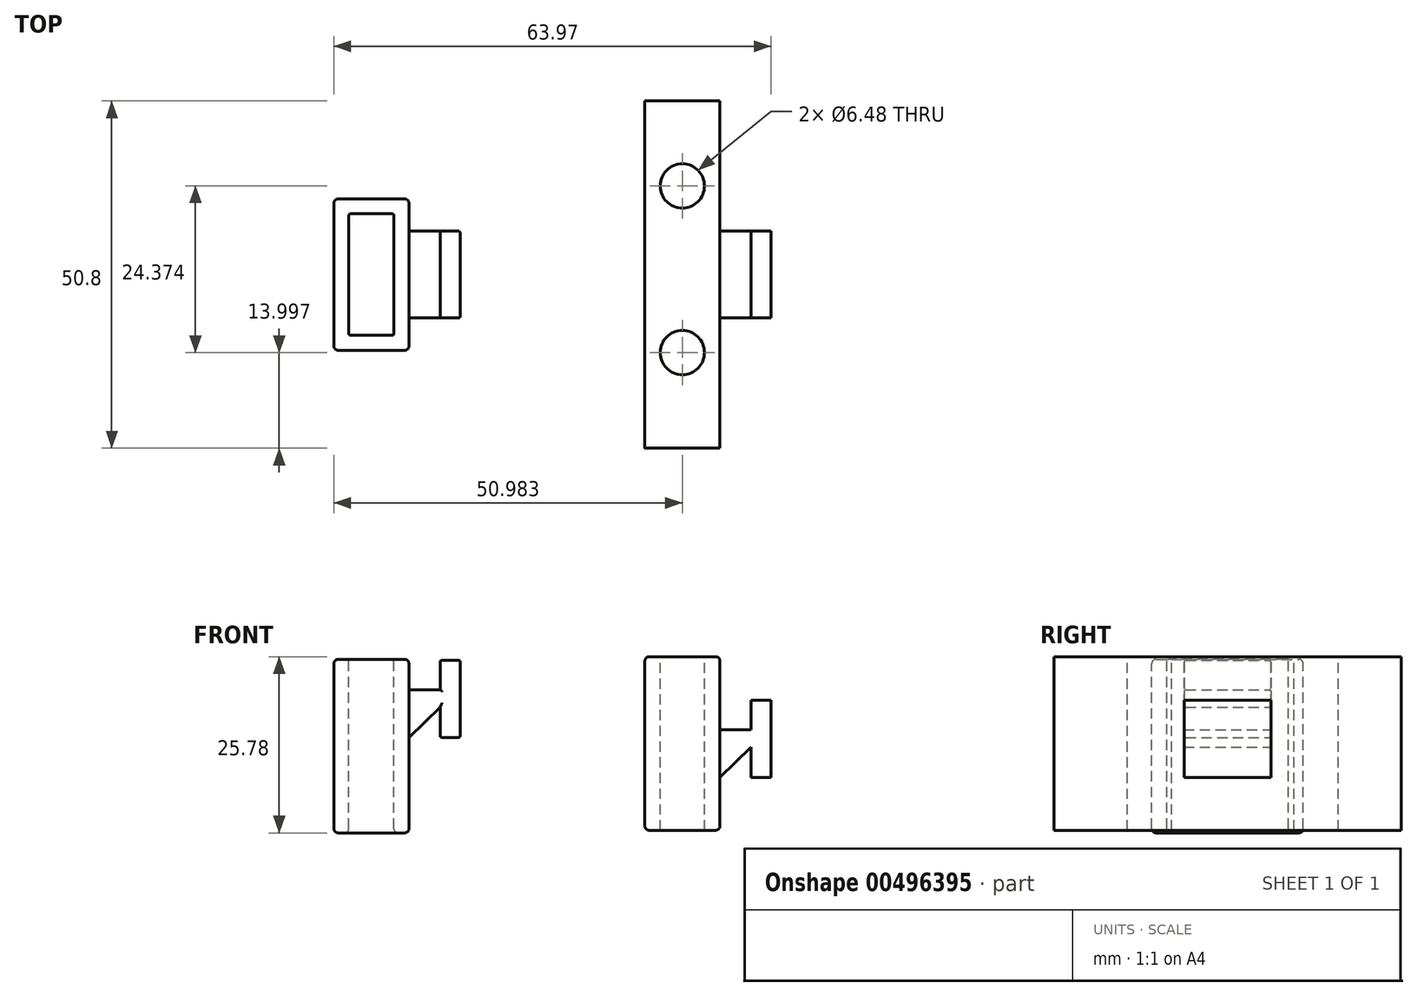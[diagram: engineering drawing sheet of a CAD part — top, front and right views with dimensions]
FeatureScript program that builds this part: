
annotation { "Feature Type Name" : "Feature", "Feature Type Description" : "" }
export const myFeature = defineFeature(function(context is Context, id is Id, definition is map)
    precondition{}
    {
        {
            var Q0;
            Q0=qCreatedBy(makeId("Front.planeOp"),FACE);
            var sketch = newSketch(context, id + "F0", { "sketchPlane" : qUnion([Q0])});
            skLineSegment(sketch, "E0", {"start": v(0, 0) * mm, "end": v(0, 11.3) * mm});
            skLineSegment(sketch, "E1", {"start": v(0, 11.3) * mm, "end": v(-2.92, 11.3) * mm});
            skLineSegment(sketch, "E2", {"start": v(-2.92, 11.3) * mm, "end": v(-2.92, 6.99) * mm});
            skLineSegment(sketch, "E3", {"start": v(-2.92, 6.99) * mm, "end": v(-7.5, 6.98) * mm});
            skLineSegment(sketch, "E4", {"start": v(-7.5, 6.99) * mm, "end": v(-7.5, 0) * mm});
            skLineSegment(sketch, "E5", {"start": v(-7.5, 0) * mm, "end": v(-2.92, 4.44) * mm});
            skLineSegment(sketch, "E6", {"start": v(-2.92, 4.44) * mm, "end": v(-2.92, 0) * mm});
            skLineSegment(sketch, "E7", {"start": v(-2.92, 0) * mm, "end": v(0, 0) * mm});
            skSolve(sketch);
        }
        {
            var Q0;
            Q0 = qSketchRegion(id + "F0", true);
            extrude(context, id + "F1", {"entities" : qUnion([Q0]), "depth" : 12.7 * mm});
        }
        {
            var Q0;
            Q0=makeQuery(id+"F1.opExtrude","CAP_FACE",FACE,{"disambiguationData":[OSD([sQuery(id+"F0.wireOp",EDGE,"E0"),sQuery(id+"F0.wireOp",EDGE,"E1"),sQuery(id+"F0.wireOp",EDGE,"E2"),sQuery(id+"F0.wireOp",EDGE,"E3"),sQuery(id+"F0.wireOp",EDGE,"E4"),sQuery(id+"F0.wireOp",EDGE,"E5"),sQuery(id+"F0.wireOp",EDGE,"E6"),sQuery(id+"F0.wireOp",EDGE,"E7")])],"isStart":true});
            var sketch = newSketch(context, id + "F2", { "sketchPlane" : qUnion([Q0])});
            skLineSegment(sketch, "E8", {"start": v(7.5, 0) * mm, "end": v(7.5, 10.8) * mm});
            skLineSegment(sketch, "E9", {"start": v(7.5, 0) * mm, "end": v(7.5, -13.34) * mm});
            skLineSegment(sketch, "E10", {"start": v(8.13, -13.97) * mm, "end": v(17.84, -13.97) * mm});
            skLineSegment(sketch, "E11", {"start": v(18.48, -13.34) * mm, "end": v(18.48, 10.8) * mm});
            skLineSegment(sketch, "E12", {"start": v(17.84, 11.43) * mm, "end": v(8.13, 11.43) * mm});
            skPoint(sketch, "E13.visualSharp", {"position": v(7.5, 11.43) * mm});
            skArc(sketch, "E13.filletArc", {"start": v(8.13, 11.43) * mm, "mid": v(7.68, 11.24) * mm, "end": v(7.5, 10.8) * mm});
            skPoint(sketch, "E14.visualSharp", {"position": v(18.48, 11.43) * mm});
            skArc(sketch, "E14.filletArc", {"start": v(18.48, 10.8) * mm, "mid": v(18.3, 11.24) * mm, "end": v(17.84, 11.43) * mm});
            skPoint(sketch, "E15.visualSharp", {"position": v(18.48, -13.97) * mm});
            skArc(sketch, "E15.filletArc", {"start": v(17.84, -13.97) * mm, "mid": v(18.3, -13.78) * mm, "end": v(18.48, -13.34) * mm});
            skPoint(sketch, "E16.visualSharp", {"position": v(7.5, -13.97) * mm});
            skArc(sketch, "E16.filletArc", {"start": v(7.5, -13.34) * mm, "mid": v(7.68, -13.78) * mm, "end": v(8.13, -13.97) * mm});
            skSolve(sketch);
        }
        {
            var Q0;
            Q0 = qSketchRegion(id + "F2", true);
            extrude(context, id + "F3", {"entities" : qUnion([Q0]), "operationType" : NewBodyOperationType.ADD, "oppositeDirection" : true, "depth" : 17.42 * mm, "hasSecondDirection" : true, "secondDirectionOppositeDirection" : false, "secondDirectionDepth" : 4.72 * mm});
        }
        {
            var Q0;
            Q0=makeQuery(id+"F3.opExtrude","SWEPT_FACE",FACE,{"disambiguationData":[OSD([sQuery(id+"F2.wireOp",EDGE,"E12")])]});
            var sketch = newSketch(context, id + "F4", { "sketchPlane" : qUnion([Q0])});
            skLineSegment(sketch, "E17.bottom", {"start": v(-16.04, 2.54) * mm, "end": v(-9.94, 2.54) * mm});
            skLineSegment(sketch, "E17.top", {"start": v(-16.04, -15.24) * mm, "end": v(-9.94, -15.24) * mm});
            skLineSegment(sketch, "E17.left", {"start": v(-16.3, 2.29) * mm, "end": v(-16.3, -14.99) * mm});
            skLineSegment(sketch, "E17.right", {"start": v(-9.7, 2.29) * mm, "end": v(-9.7, -14.99) * mm});
            skPoint(sketch, "E18.visualSharp", {"position": v(-16.3, 2.54) * mm});
            skArc(sketch, "E18.filletArc", {"start": v(-16.04, 2.54) * mm, "mid": v(-16.22, 2.47) * mm, "end": v(-16.3, 2.29) * mm});
            skPoint(sketch, "E19.visualSharp", {"position": v(-9.7, 2.54) * mm});
            skArc(sketch, "E19.filletArc", {"start": v(-9.7, 2.29) * mm, "mid": v(-9.76, 2.47) * mm, "end": v(-9.94, 2.54) * mm});
            skPoint(sketch, "E20.visualSharp", {"position": v(-16.3, -15.24) * mm});
            skArc(sketch, "E20.filletArc", {"start": v(-16.3, -14.99) * mm, "mid": v(-16.22, -15.17) * mm, "end": v(-16.04, -15.24) * mm});
            skPoint(sketch, "E21.visualSharp", {"position": v(-9.7, -15.24) * mm});
            skArc(sketch, "E21.filletArc", {"start": v(-9.94, -15.24) * mm, "mid": v(-9.76, -15.17) * mm, "end": v(-9.7, -14.99) * mm});
            skSolve(sketch);
        }
        {
            var Q0;
            Q0 = qSketchRegion(id + "F4", true);
            extrude(context, id + "F5", {"entities" : qUnion([Q0]), "operationType" : NewBodyOperationType.REMOVE, "endBound" : BoundingType.THROUGH_ALL, "oppositeDirection" : true, "depth" : 25.4 * mm});
        }
        {
            var Q0;
            Q0=qCreatedBy(makeId("Front.planeOp"),FACE);
            var sketch = newSketch(context, id + "F6", { "sketchPlane" : qUnion([Q0])});
            skLineSegment(sketch, "E22", {"start": v(45.5, -5.85) * mm, "end": v(45.5, 5.46) * mm});
            skLineSegment(sketch, "E23", {"start": v(45.5, 5.46) * mm, "end": v(42.57, 5.46) * mm});
            skLineSegment(sketch, "E24", {"start": v(42.57, 5.46) * mm, "end": v(42.57, 1.14) * mm});
            skLineSegment(sketch, "E25", {"start": v(42.57, 1.14) * mm, "end": v(38, 1.14) * mm});
            skLineSegment(sketch, "E26", {"start": v(38, 1.14) * mm, "end": v(38, -5.85) * mm});
            skLineSegment(sketch, "E27", {"start": v(38, -5.85) * mm, "end": v(42.57, -1.4) * mm});
            skLineSegment(sketch, "E28", {"start": v(42.57, -1.4) * mm, "end": v(42.57, -5.85) * mm});
            skLineSegment(sketch, "E29", {"start": v(42.57, -5.85) * mm, "end": v(45.5, -5.85) * mm});
            skSolve(sketch);
        }
        {
            var Q0;
            Q0 = qSketchRegion(id + "F6", true);
            extrude(context, id + "F7", {"entities" : qUnion([Q0]), "depth" : 12.7 * mm});
        }
        {
            var Q0;
            Q0=makeQuery(id+"F7.opExtrude","CAP_FACE",FACE,{"disambiguationData":[OSD([sQuery(id+"F6.wireOp",EDGE,"E22"),sQuery(id+"F6.wireOp",EDGE,"E23"),sQuery(id+"F6.wireOp",EDGE,"E24"),sQuery(id+"F6.wireOp",EDGE,"E25"),sQuery(id+"F6.wireOp",EDGE,"E26"),sQuery(id+"F6.wireOp",EDGE,"E27"),sQuery(id+"F6.wireOp",EDGE,"E28"),sQuery(id+"F6.wireOp",EDGE,"E29")])],"isStart":false});
            var sketch = newSketch(context, id + "F8", { "sketchPlane" : qUnion([Q0])});
            skLineSegment(sketch, "E30", {"start": v(27.02, 0.38) * mm, "end": v(27.02, 11.18) * mm});
            skLineSegment(sketch, "E31", {"start": v(27.02, 0.38) * mm, "end": v(27.02, -12.95) * mm});
            skLineSegment(sketch, "E32", {"start": v(27.65, -13.59) * mm, "end": v(37.37, -13.59) * mm});
            skLineSegment(sketch, "E33", {"start": v(38, -12.95) * mm, "end": v(38, 11.18) * mm});
            skLineSegment(sketch, "E34", {"start": v(37.37, 11.81) * mm, "end": v(27.65, 11.81) * mm});
            skPoint(sketch, "E35.visualSharp", {"position": v(27.02, 11.81) * mm});
            skArc(sketch, "E35.filletArc", {"start": v(27.65, 11.81) * mm, "mid": v(27.2, 11.63) * mm, "end": v(27.02, 11.18) * mm});
            skPoint(sketch, "E36.visualSharp", {"position": v(38, 11.81) * mm});
            skArc(sketch, "E36.filletArc", {"start": v(38, 11.18) * mm, "mid": v(37.82, 11.63) * mm, "end": v(37.37, 11.81) * mm});
            skPoint(sketch, "E37.visualSharp", {"position": v(38, -13.59) * mm});
            skArc(sketch, "E37.filletArc", {"start": v(37.37, -13.59) * mm, "mid": v(37.82, -13.4) * mm, "end": v(38, -12.95) * mm});
            skPoint(sketch, "E38.visualSharp", {"position": v(27.02, -13.59) * mm});
            skArc(sketch, "E38.filletArc", {"start": v(27.02, -12.95) * mm, "mid": v(27.2, -13.4) * mm, "end": v(27.65, -13.59) * mm});
            skSolve(sketch);
        }
        {
            var Q0;
            Q0 = qSketchRegion(id + "F8", true);
            extrude(context, id + "F9", {"entities" : qUnion([Q0]), "operationType" : NewBodyOperationType.ADD, "depth" : 19.05 * mm, "hasSecondDirection" : true, "secondDirectionOppositeDirection" : true, "secondDirectionDepth" : 31.75 * mm});
        }
        {
            var Q0;
            Q0=makeQuery(id+"F9.opExtrude","SWEPT_FACE",FACE,{"disambiguationData":[OSD([sQuery(id+"F8.wireOp",EDGE,"E34")])]});
            var sketch = newSketch(context, id + "F10", { "sketchPlane" : qUnion([Q0])});
            skCircle(sketch, "E39", {"center": v(32.5, 6.62) * mm, "radius": 3.24 * mm});
            skCircle(sketch, "E40", {"center": v(32.5, -17.75) * mm, "radius": 3.24 * mm});
            skSolve(sketch);
        }
        {
            var Q0;
            Q0 = qSketchRegion(id + "F10", true);
            extrude(context, id + "F11", {"entities" : qUnion([Q0]), "operationType" : NewBodyOperationType.REMOVE, "endBound" : BoundingType.THROUGH_ALL, "oppositeDirection" : true, "depth" : 25.4 * mm});
        }
        {
            var Q0;
            Q0=makeQuery(id+"F3.opExtrude","CAP_EDGE",EDGE,{"disambiguationData":[OSD([sQuery(id+"F2.wireOp",EDGE,"E11")])],"isStart":false});
            var Q1;
            Q1=makeQuery(id+"F3.opExtrude","CAP_EDGE",EDGE,{"disambiguationData":[OSD([sQuery(id+"F2.wireOp",EDGE,"E11")])],"isStart":true});
            fillet(context, id + "F12", {"entities" : qUnion([Q0, Q1]), "radius" : 0.64 * mm, "tangentPropagation" : true, "allowEdgeOverflow" : false});
        }
        {
            var Q0;
            Q0=makeQuery(id+"F1.opExtrude","SWEPT_EDGE",EDGE,{"disambiguationData":[OSD([sQuery(id+"F0.wireOp",EDGE,"E0"),sQuery(id+"F0.wireOp",EDGE,"E1")])]});
            var Q1;
            Q1=makeQuery(id+"F1.opExtrude","SWEPT_EDGE",EDGE,{"disambiguationData":[OSD([sQuery(id+"F0.wireOp",EDGE,"E0"),sQuery(id+"F0.wireOp",EDGE,"E7")])]});
            var Q2;
            Q2=makeQuery(id+"F1.opExtrude","SWEPT_EDGE",EDGE,{"disambiguationData":[OSD([sQuery(id+"F0.wireOp",EDGE,"E1"),sQuery(id+"F0.wireOp",EDGE,"E2")])]});
            var Q3;
            Q3=makeQuery(id+"F1.opExtrude","SWEPT_EDGE",EDGE,{"disambiguationData":[OSD([sQuery(id+"F0.wireOp",EDGE,"E6"),sQuery(id+"F0.wireOp",EDGE,"E7")])]});
            fillet(context, id + "F13", {"entities" : qUnion([Q0, Q1, Q2, Q3]), "radius" : 0.25 * mm, "tangentPropagation" : true, "allowEdgeOverflow" : false});
        }
        {
            var Q0;
            Q0=makeQuery(id+"F1.opExtrude","CAP_EDGE",EDGE,{"disambiguationData":[OSD([sQuery(id+"F0.wireOp",EDGE,"E7")])],"isStart":false});
            var Q1;
            {var subQ0=sQuery(id+"F0.wireOp",EDGE,"E7");var subQ1=sQuery(id+"F0.wireOp",EDGE,"E0");Q1=makeQuery(id+"F13.opFillet","BLEND_EDGE",EDGE,{"blendedFrom":[makeQuery(id+"F1.opExtrude","SWEPT_EDGE",EDGE,{"disambiguationData":[OSD([subQ1,subQ0])]}),makeQuery(id+"F1.opExtrude","CAP_FACE",FACE,{"disambiguationData":[OSD([subQ1,sQuery(id+"F0.wireOp",EDGE,"E1"),sQuery(id+"F0.wireOp",EDGE,"E2"),sQuery(id+"F0.wireOp",EDGE,"E3"),sQuery(id+"F0.wireOp",EDGE,"E4"),sQuery(id+"F0.wireOp",EDGE,"E5"),sQuery(id+"F0.wireOp",EDGE,"E6"),subQ0])],"isStart":false})],"blendedInto":[makeQuery(id+"F1.opExtrude","CAP_FACE",FACE,{"disambiguationData":[OSD([subQ1,sQuery(id+"F0.wireOp",EDGE,"E1"),sQuery(id+"F0.wireOp",EDGE,"E2"),sQuery(id+"F0.wireOp",EDGE,"E3"),sQuery(id+"F0.wireOp",EDGE,"E4"),sQuery(id+"F0.wireOp",EDGE,"E5"),sQuery(id+"F0.wireOp",EDGE,"E6"),subQ0])],"isStart":false})]});}
            var Q2;
            Q2=makeQuery(id+"F1.opExtrude","CAP_EDGE",EDGE,{"disambiguationData":[OSD([sQuery(id+"F0.wireOp",EDGE,"E5")])],"isStart":false});
            var Q3;
            Q3=makeQuery(id+"F1.opExtrude","CAP_EDGE",EDGE,{"disambiguationData":[OSD([sQuery(id+"F0.wireOp",EDGE,"E3")])],"isStart":false});
            var Q4;
            Q4=makeQuery(id+"F1.opExtrude","CAP_EDGE",EDGE,{"disambiguationData":[OSD([sQuery(id+"F0.wireOp",EDGE,"E0")])],"isStart":true});
            var Q5;
            Q5=makeQuery(id+"F1.opExtrude","CAP_EDGE",EDGE,{"disambiguationData":[OSD([sQuery(id+"F0.wireOp",EDGE,"E5")])],"isStart":true});
            var Q6;
            Q6=makeQuery(id+"F1.opExtrude","CAP_EDGE",EDGE,{"disambiguationData":[OSD([sQuery(id+"F0.wireOp",EDGE,"E3")])],"isStart":true});
            fillet(context, id + "F14", {"entities" : qUnion([Q0, Q1, Q2, Q3, Q4, Q5, Q6]), "radius" : 0.25 * mm, "tangentPropagation" : true, "allowEdgeOverflow" : false});
        }
        {
            var Q0;
            Q0=makeQuery(id+"F5.boolean.opBoolean","COPY",EDGE,{"derivedFrom":makeQuery(id+"F5.opExtrude","CAP_EDGE",EDGE,{"disambiguationData":[OSD([sQuery(id+"F4.wireOp",EDGE,"E17.bottom")])],"isStart":true})});
            var Q1;
            Q1=makeQuery(id+"F5.boolean.opBoolean","INTERSECT",EDGE,{"derivedFrom":[makeQuery(id+"F3.opExtrude","SWEPT_FACE",FACE,{"disambiguationData":[OSD([sQuery(id+"F2.wireOp",EDGE,"E10")])]}),makeQuery(id+"F5.opExtrude","SWEPT_FACE",FACE,{"disambiguationData":[OSD([sQuery(id+"F4.wireOp",EDGE,"E17.right")])]})]});
            fillet(context, id + "F15", {"entities" : qUnion([Q0, Q1]), "radius" : 0.64 * mm, "tangentPropagation" : true, "allowEdgeOverflow" : false});
        }
    });
